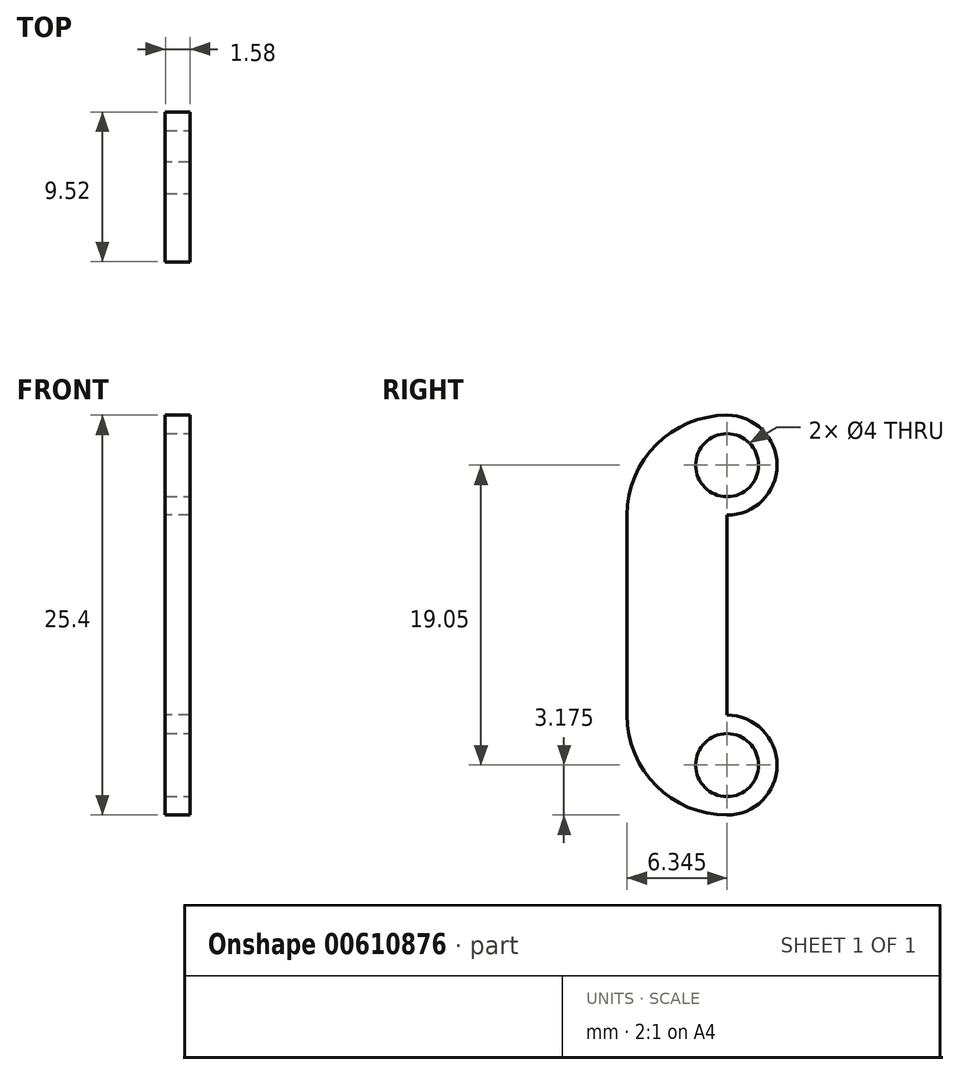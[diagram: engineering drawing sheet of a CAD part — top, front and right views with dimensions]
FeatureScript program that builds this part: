
annotation { "Feature Type Name" : "Feature", "Feature Type Description" : "" }
export const myFeature = defineFeature(function(context is Context, id is Id, definition is map)
    precondition{}
    {
        {
            var Q0;
            Q0=qCreatedBy(makeId("Right.planeOp"),FACE);
            var sketch = newSketch(context, id + "F0", { "sketchPlane" : qUnion([Q0])});
            skLineSegment(sketch, "E0.bottom", {"start": v(3.18, 12.7) * mm, "end": v(3.18, 12.7) * mm});
            skLineSegment(sketch, "E0.top", {"start": v(3.18, -12.7) * mm, "end": v(3.17, -12.7) * mm});
            skLineSegment(sketch, "E0.left", {"start": v(-3.17, 6.35) * mm, "end": v(-3.17, -6.35) * mm});
            skLineSegment(sketch, "E0.right", {"start": v(3.18, 6.35) * mm, "end": v(3.17, -6.35) * mm});
            skLineSegment(sketch, "E1", {"start": v(-3.18, 0) * mm, "end": v(0, 0) * mm, "construction": true});
            skLineSegment(sketch, "E2", {"start": v(0, 0) * mm, "end": v(3.17, 0) * mm, "construction": true});
            skArc(sketch, "E3", {"start": v(3.18, 6.35) * mm, "mid": v(6.35, 9.53) * mm, "end": v(3.18, 12.7) * mm});
            skArc(sketch, "E4", {"start": v(3.17, -12.7) * mm, "mid": v(6.35, -9.53) * mm, "end": v(3.17, -6.35) * mm});
            skPoint(sketch, "E5.visualSharp", {"position": v(-3.18, -12.7) * mm});
            skArc(sketch, "E5.filletArc", {"start": v(-3.17, -6.35) * mm, "mid": v(-1.32, -10.84) * mm, "end": v(3.18, -12.7) * mm});
            skPoint(sketch, "E6.visualSharp", {"position": v(-3.18, 12.7) * mm});
            skArc(sketch, "E6.filletArc", {"start": v(3.17, 12.7) * mm, "mid": v(-1.32, 10.84) * mm, "end": v(-3.17, 6.35) * mm});
            skSolve(sketch);
        }
        {
            var Q0;
            Q0=makeQuery(id+"F0.imprint","IMPRINT",FACE,{"disambiguationData":[TD([[makeQuery(id+"F0.imprint","IMPRINT",EDGE,{"derivedFrom":sQuery(id+"F0.wireOp",EDGE,"E0.left")}),1.0]])]});
            extrude(context, id + "F1", {"entities" : qUnion([Q0]), "endBound" : BoundingType.SYMMETRIC, "depth" : 1.59 * mm, "offsetDistance" : 25.4 * mm});
        }
        {
            var Q0;
            Q0=makeQuery(id+"F1.opExtrude","CAP_FACE",FACE,{"disambiguationData":[OSD([sQuery(id+"F0.wireOp",EDGE,"E0.left"),sQuery(id+"F0.wireOp",EDGE,"E0.right"),sQuery(id+"F0.wireOp",EDGE,"E3"),sQuery(id+"F0.wireOp",EDGE,"E4"),sQuery(id+"F0.wireOp",EDGE,"E5.filletArc"),sQuery(id+"F0.wireOp",EDGE,"E6.filletArc")])],"isStart":false});
            var sketch = newSketch(context, id + "F2", { "sketchPlane" : qUnion([Q0])});
            skPoint(sketch, "E7", {"position": v(3.18, 9.53) * mm});
            skPoint(sketch, "E8", {"position": v(3.17, -9.53) * mm});
            skSolve(sketch);
        }
        {
            var Q0;
            Q0=sQuery(id+"F2.wireOp",VERTEX,"E7");
            var Q1;
            Q1=sQuery(id+"F2.wireOp",VERTEX,"E8");
            var Q2;
            Q2=makeQuery(id+"F1.opExtrude","SWEPT_BODY",BODY,{"disambiguationData":[OSD([sQuery(id+"F0.wireOp",EDGE,"E0.left"),sQuery(id+"F0.wireOp",EDGE,"E0.right"),sQuery(id+"F0.wireOp",EDGE,"E3"),sQuery(id+"F0.wireOp",EDGE,"E4"),sQuery(id+"F0.wireOp",EDGE,"E5.filletArc"),sQuery(id+"F0.wireOp",EDGE,"E6.filletArc")])]});
            hole(context, id + "F3", {"style" : HoleStyle.SIMPLE, "endStyle" : HoleEndStyle.THROUGH, "holeDiameter" : 4 * mm, "majorDiameter" : 6.35 * mm, "isTappedThrough" : true, "tappedDepth" : 12.7 * mm, "tapClearance" : 3, "locations" : qUnion([Q0, Q1]), "scope" : qUnion([Q2])});
        }
    });
